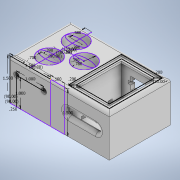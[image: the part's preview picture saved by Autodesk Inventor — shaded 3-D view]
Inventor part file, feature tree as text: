
AUTODESK INVENTOR PART (.ipt)
format: ipt  version: 2020 (Build 240168000, 168)  size: 339,456 bytes
history: native  units: in
note: dims shown in document units (in); Inventor stores cm internally (conversion verified against a paired STEP export)
features: extrude x10, sketch x7, hole x1, fillet x1
ambient origin geometry x8: Origin, YZ Plane, XZ Plane, XY Plane, X Axis, Y Axis, Z Axis, Center Point
bodies: Solid1 (feature_tree)
feature tree (19):
  extrude  "Extrusion1"  Depth=1.5in
  hole  "Hole1"  [1 undecoded]
  sketch  "Sketch2"  dims[d0=1.5in d1=1.5in]
  extrude  "Extrusion2"  TaperAngle=90.0deg  [1 undecoded]
  extrude  "Extrusion3"  Depth=2.24in TaperAngle=0.0deg
  extrude  "Extrusion4"  Depth=0.7in
  extrude  "Extrusion5"  Depth=0.39in
  extrude  "Extrusion6"  Depth=1.0in
  extrude  "Extrusion7"  TaperAngle=180.0deg  [1 undecoded]
  sketch  "Sketch7"  dims[d9=0.201in d10=0.75in d11=0.438in d12=0.25in d13=0.5635in d14=0.5in d15=0.0in d16=0.7in]
  extrude  "Extrusion8"  Depth=0.39in
  extrude  "Extrusion9"  TaperAngle=180.0deg  [1 undecoded]
  extrude  "Extrusion10"  Depth=1.25in TaperAngle=0.0deg
  sketch  "Sketch9"  dims[d19=90.0deg d20=0.2in d21=180.0deg d22=0.39in d23=180.0deg d24=1.25in d25=0.0in d26=1.5in d27=0.0in d28=0.15in d29=0.15in d30=0.25in d31=0.0in d32=0.58in d34=1.5in d35=0.5in d36=0.4in d37=0.39in d38=0.78in d39=0.15in d40=0.125in d41=0.15in d42=0.15in d43=0.15in d44=0.15in d45=90.0deg d46=1.5in d47=0.0in d48=0.15in d49=0.0in d50=1.0in d51=0.25in d52=0.15in d53=0.0in d54=0.2in d55=135.0deg d56=0.2in d57=45.0deg d58=0.15in d59=0.0in d60=0.075in d61=0.0in d62=0.75in d63=0.45in d64=0.8in d65=0.1in d66=1.0in d67=1.0in d68=0.0in]
  fillet  "Fillet1"  Radius=1.5in
  sketch  "Sketch4"  dims[d2=0.25in d3=90.0deg]
  sketch  "Sketch5"  dims[d4=1.0in d5=90.0deg]
  sketch  "Sketch6"  dims[d6=1.0in d7=2.24in d8=0.0in]
  sketch  "Sketch8"  dims[d17=90.0deg d18=0.39in]
note: 4 required parameter values undecoded (feature->parameter linkage not recoverable at this tier; creation-order binding heuristic only, values carry confidence <= 0.55)
